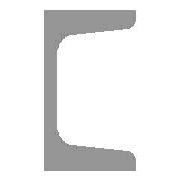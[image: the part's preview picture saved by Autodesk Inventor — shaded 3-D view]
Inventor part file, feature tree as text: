
AUTODESK INVENTOR PART (.ipt)
format: ipt  version: 2024 (Build 280153000, 153)  size: 151,552 bytes
history: native  units: mm (DEFAULTED — no unit token found)
features: sketch x5, other x4, hole x4, plane x1
ambient origin geometry x8: Origin, YZ Plane, XZ Plane, XY Plane, X Axis, Y Axis, Z Axis, Center Point
bodies: Solid1 (feature_tree), Body (feature_tree)
feature tree (14):
  parser-record x1  (decoder bookkeeping rows leaked as tree rows — omitted from the tree; the rows remain in map.json)
  other  "Driven Length"
  other  "Start Plane"
  other  "End Plane"
  hole  "Hole1"  [1 undecoded]
  hole  "Hole2"  [1 undecoded]
  hole  "Hole3"  [1 undecoded]
  hole  "Hole4"  [1 undecoded]
  sketch  "Sketch3"  dims[d0=9.2mm d1=125.0mm]
  plane  "Work Plane3"
  sketch  "Sketch5"  dims[d2=85.0mm d3=13.0mm]
  sketch  "Sketch6"  dims[d4=37.9mm d5=3.983442mm]
  sketch  "Sketch7"  dims[d6=500.0mm d7=0.0mm d23=13.5mm]
  sketch  "Sketch8"  dims[d24=7.0mm d25=2.2mm d26=-0.0mm d27=500.0mm d28=90.0deg d29=500.0mm d30=17.5mm d31=6.0mm d32=4.0mm d33=2.0mm d34=90.0deg d35=8.0mm d36=0.0mm d37=17.5mm d38=6.0mm d39=4.0mm d40=2.0mm d41=90.0deg d42=8.0mm d43=0.0mm d44=17.5mm d45=6.0mm d46=4.0mm d47=2.0mm d48=90.0deg d49=8.0mm d50=0.0mm d51=17.5mm d52=6.0mm d53=4.0mm d54=2.0mm d55=90.0deg d56=8.0mm d57=0.0mm]
note: 4 required parameter values undecoded (feature->parameter linkage not recoverable at this tier; creation-order binding heuristic only, values carry confidence <= 0.55)
